# Revit family: ITK 19 вентиляционный модуль 1U 2 вентилятора с цифровым термостатом
name_source: partatom
category: Электрооборудование
revit_build: Autodesk Revit 2016 (Build: 20160314_0715(x64)
units: mm (PartAtom-declared; Revit-internal decimal feet)

## family parameters
Всегда вертикально = Да
На основе рабочей плоскости = Нет
Общий = Нет
При загрузке вырезать с полостями = Нет
Размер круглого соединителя = Использовать диаметр
Тип детали = Другая панель
Точка расчета площади = Нет

## types (1)
- FM05-1U2TS
    ADSK_Единица измерения = шт
    ADSK_Завод-изготовитель = IEK
    ADSK_Классификация нагрузок = Прочее
    ADSK_Количество фаз = 1
    ADSK_Количество фаз числовое = 1
    ADSK_Коэффициент мощности = 1
    ADSK_Марка = FM05-1U2TS
    ADSK_Масса = 0
    ADSK_Наименование = ITK 19" вентил. модуль 1U 2 вентилятора с цифровым термостатом
    ADSK_Наименование краткое = FM05-1U2TS
    ADSK_Напряжение = 220 В
    ADSK_Номинальная мощность = 0 Вт
    ADSK_Полная мощность = 0 В·А
    ADSK_Ток = 0 А
    URL = http://www.itk-group.ru
    Высота = 44 мм
    Глубина = 171 мм
    Изготовитель = ITK
    Комментарии к типоразмеру = FM05-1U2TS
    Материал = Окраска - RAL 9005
    Описание = Потолочные вентиляторные панели предназначены для установки и использования в серверных шкафах LINEA S для организации принудительного охлаждения и вентиляции установленного в них активного оборудования и вывода из шкафа горячего воздуха.

Потолочные панели имеют два или четыре вентиляторных модуля и в зависимости от модели могут оснащаться биметаллическим термостатом (тип NO).
Диапазон регулировки температуры термостата: от 0 до 60°С.
Номинальное рабочее напряжение: 230В. Частота тока: 50Гц.
Минимальный срок службы: 50 тыс. часов.
Подача рабочего напряжения на вентиляторную панель осуществляется через встроенный разъем питания С14 10А/250В. 

Внимание! Кабель электропитания для подключения к сети в комплект поставки не входит.

Вентиляторные панели устанавливаются в крыше шкафа на специально предусмотренное посадочное место и не занимают полезной высоты 19-дюймовых монтажных профилей. Корпус панели предусматривает организацию защитного заземления.
В шкаф LINEA S можно установить только одну вентиляторную панель на 2 или на 4 модуля.
Совместимы со всеми 19-дюймовым шкафами и стойками ITK.
Обладают современным привлекательным дизайном и продуманной конструкцией.
Удобны в монтаже и эксплуатации.
Соответствие международным стандартам ISO9001, IEC 297, ISO/IEC 11801. 
Сертифицированы по ГОСТ Р.
Все аксессуары идут с крепежом.
Возможно исполнение в двух цветах: серый (RAL7035) и черный (RAL9005).
Всегда в наличии на складе.
Гарантия на все аксессуары до 2-х лет
    Ширина = 483 мм
